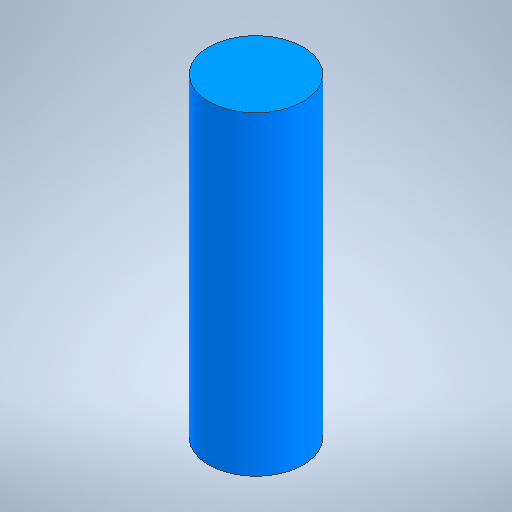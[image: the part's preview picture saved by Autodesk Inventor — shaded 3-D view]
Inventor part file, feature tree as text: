
AUTODESK INVENTOR PART (.ipt)
format: ipt  version: 2025.2 (Build 292293000, 293)  size: 261,120 bytes
history: native  units: mm
features: extrude x1, sketch x1
ambient origin geometry x8: Origin, YZ Plane, XZ Plane, XY Plane, X Axis, Y Axis, Z Axis, Center Point
bodies: Solid1 (feature_tree)
feature tree (2):
  extrude  "Extrusion1"  Depth=70.0mm TaperAngle=0.0deg
  sketch  "Sketch1"  dims[d0=21.0mm d1=70.0mm d2=0.0mm]
